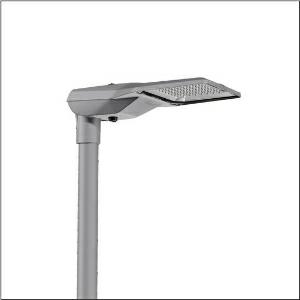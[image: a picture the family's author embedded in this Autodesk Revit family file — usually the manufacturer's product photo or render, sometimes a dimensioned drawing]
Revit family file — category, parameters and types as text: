
# Revit family: streetlight_sl_21_midi___st1_0a_5xe3d23t08lb_1be3
name_source: partatom
category: Lighting Fixtures
units: mm (PartAtom-declared; Revit-internal decimal feet)

## family parameters
Cut with Voids When Loaded = No
Host = Face
Light Source = No
Part Type = Normal
Room Calculation Point = No
Round Connector Dimension = Use Diameter
Shared = No

## types (1)
- --- (1 x LED, 11880 lm, 99.6 W, 2200K)
    Apparent Load = 100 VA
    CIE Flux Codes = 37 72 97 100 100
    Color Rendering = 70
    Color Temperature = 2200K
    Default Elevation = 1800 mm
    Description = Streetlight SL 21 midi, mast luminaire, primary light control with lens, of PMMA, primary optical cover: cover, of toughened safety glass, transparent, light distribution: ST1.0a, light emission: direct distribution, primary light characteristic: asymmetric, installation type: side-entry, post-top, LED, High Power LED, rated luminous flux: 11.880lm, luminous efficacy: 119lm/W, light colour: 722, colour temperature: 2200K, control gear: D4i, control: overheat protection, constant luminous flux control, time-dependent luminous flux control, flexible luminous flux parameterisation, pre-setting: logarithmic dimming characteristic, mains connection: 230..240V, AC, 50/60Hz, start of lifetime: 100W, end of service life: 102W, reduction: 45W, luminaire housing, of diecast aluminium, powder-coated, SITECO metallic grey (DB 702S), corrosivity category C5 high according to DIN EN ISO 12944, please order mast flange separately, inclination adjustable: 0°, 5°, 10°, 15°, sealing non-destructively replaceable, multi-level sealing system, length: 644mm, width: 335mm, height: 110mm, mast flange for spigot size: 42mm (side-entry): 5XC10008XM4, 60/48mm (side-entry/post-top): 5XC10108XM2, 76/60mm (side-entry/post-top): 5XC10108XM1, mounting height: 4..8m, Smart Interface below and above, protection rating (complete): IP66, insulation class (complete): insulation class II (safety insulation), certification: CE, ENEC, ENEC+, VDE, impact resistance: IK10, permissible operating ambient temperature for outdoor applications: -40..+50°C, standard-compliant lighting for roads and squares, packaging unit: 1 piece

Light Distribution: ST1.0a
    Height = 111 mm
    Lamp = 1 x LED
    Lamp Light Flux = 11880 lm
    Lamp Power = 99.6 W
    Lamp count = 1
    Length = 644 mm
    Luminous efficacy = 119 lm/W
    Manufacturer = Siteco
    ModVariant = No
    Model = 5XE3D23T08LB
    Number of Poles = 1
    OnlyDefault = Yes
    Power Factor = 1
    Product Name = Streetlight SL 21 midi | ST1.0a
    Product group = mast luminaire | pylon top
    ProductGroupID = 6100
    Protection Class = Protection class II
    Protection Degree = IP 66
    RLX_Detail_Level = 1
    RLX_Emergency_Light_Flux = 0 lm
    RLX_Emergency_Type = 0
    RLX_Emergency_Type_DB = No
    RlxData = <blob elided: 26945 chars, md5=f1db932c>
    Socket = socket
    Standby Power = 0 W
    System Light Flux = 11880 lm
    System Power = 100 W
    Type Comments = factory setting: luminous flux: 100 % | dim-lin: 254 | 1020 mA
    Type Image = l_1004304.jpg
    URL = http://relux.com
    VarID = @adj_031843
    Voltage = 0 V
    Weight = 0.00 kg
    Width = 336 mm

## geometry (parser evidence)
native form markers: Blend x4, Sweep x13
no freeform markers — native parametric forms only
